# Revit family: Building-ConnessioniIEC309-GEWISS-IEC309HP-PRESA_FISSA_INC_ST_TEDESCO
name_source: partatom
category: Apparecchi elettrici
units: mm (PartAtom-declared; Revit-internal decimal feet)

## family parameters
Condiviso = No
Host = Superficie
Mantenere orientamento annotazione = Sì
Punto di calcolo locali = Sì
Quota connettore circolare = Usa diametro
Taglio con vuoti quando caricato = No
Tipo di parte = Normale

## types (1)
- Building-ConnessioniIEC309-GEWISS-IEC309HP-PRESA_FISSA_INC_ST_TEDESCO
    BLOCCO = B=C
    Catalogo = BUILDING
    Colore: = Blu
    Corpo centrale = Default(2)
    Corrente nominale (A) = 16
    Descrizione = PRESA SCHUKO IP54 230V CON FLANGIA
    Dimensioni flangia (mm) = 50x50
    FORMULA = 1000 mm  [stored 3.28084 ft]
    Frequenza = 50/60 Hz
    Glow wire test: = 850 °C (Parti attive) - 650 °C (Parti passive)
    Grado di protezione = IP54
    IDF = 85c9a43b-b8e2-4230-9196-0c04cab01744
    IDT = 49630d0f696a4c5082891f2d21ac5637
    Immagine tipo = <Nessuno>
    L = 155 mm
    Modello = GW62393
    N. poli = 2P+T
    Piastra = Default(2)
    Produttore = GEWISS S.p.A.
    Prospetto di default = 500 mm
    SEO = Presa
    SPinotto = Default(2)
    Scheda Tecnica = https://www.gewiss.com
    Sportello_visibile = Sì
    Spostamento_S = 957 mm
    Standard = Tedesco
    Temperatura di utilizzo = -25 +55 °C
    Tensione nominale = 230V
    Termopressione con biglia = 125 °C (Parti attive) - 80 °C (Parti passive)
    Tipo Cablaggio = A vite
    URL = https://www.gewiss.com
    Versione file RFA = 21.11
    W = 115 mm

note: [stored X ft] marks values corroborated as IEEE doubles in the binary element streams (Revit-internal decimal feet)

## geometry (parser evidence)
native form markers: Sweep x2
no freeform markers — native parametric forms only
